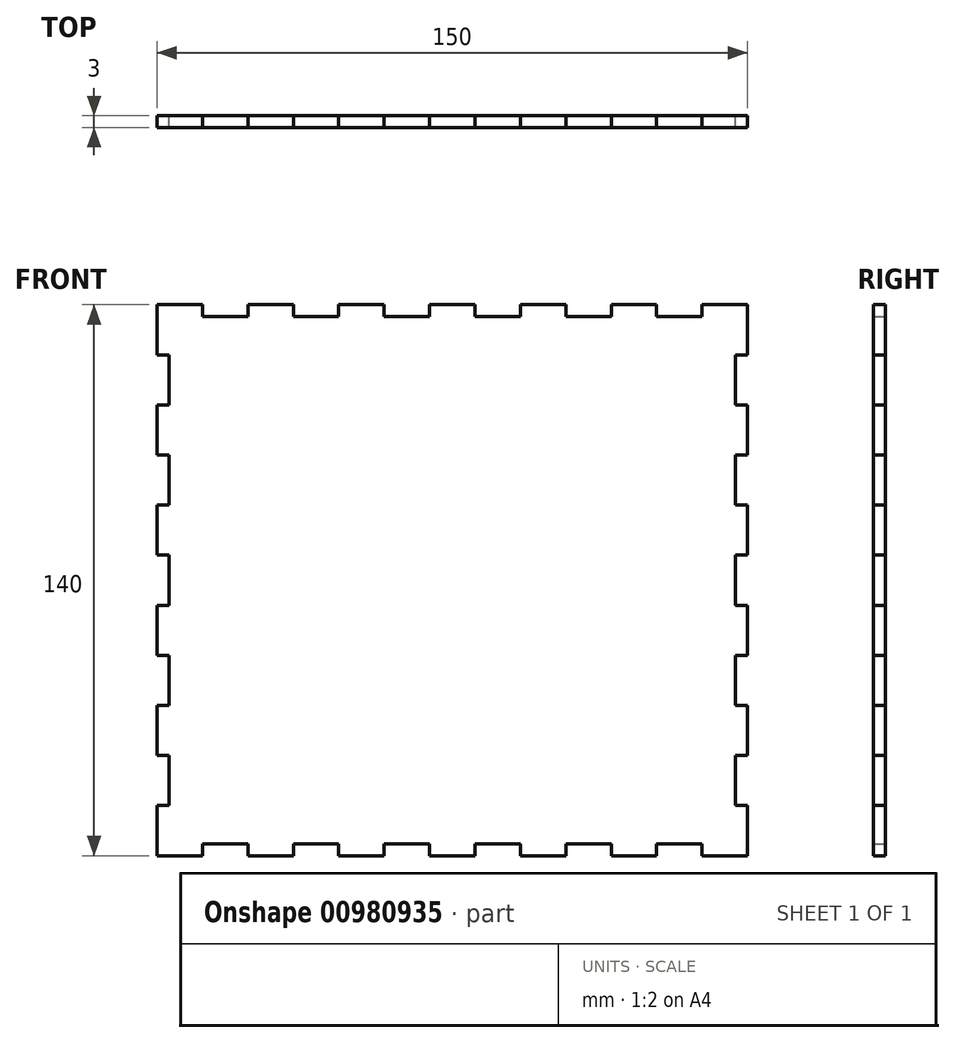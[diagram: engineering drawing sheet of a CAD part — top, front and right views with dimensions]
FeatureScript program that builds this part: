
annotation { "Feature Type Name" : "Feature", "Feature Type Description" : "" }
export const myFeature = defineFeature(function(context is Context, id is Id, definition is map)
    precondition{}
    {
        {
            var Q0;
            Q0=qCreatedBy(makeId("Front.planeOp"),FACE);
            var sketch = newSketch(context, id + "F0", { "sketchPlane" : qUnion([Q0])});
            skPoint(sketch, "E0.middle", {"position": v(0, 0) * mm});
            skLineSegment(sketch, "E1", {"start": v(75, 70) * mm, "end": v(75, 57.27) * mm});
            skLineSegment(sketch, "E2", {"start": v(75, 57.27) * mm, "end": v(72, 57.27) * mm});
            skLineSegment(sketch, "E3", {"start": v(72, 57.27) * mm, "end": v(72, 44.55) * mm});
            skLineSegment(sketch, "E4", {"start": v(72, 44.55) * mm, "end": v(75, 44.55) * mm});
            skLineSegment(sketch, "E5", {"start": v(75, 44.55) * mm, "end": v(75, 31.82) * mm});
            skLineSegment(sketch, "E6.1.0.1", {"start": v(75, 19.1) * mm, "end": v(75, 6.36) * mm});
            skLineSegment(sketch, "E6.1.0.2", {"start": v(72, 31.82) * mm, "end": v(72, 19.1) * mm});
            skLineSegment(sketch, "E6.1.0.3", {"start": v(72, 19.1) * mm, "end": v(75, 19.1) * mm});
            skLineSegment(sketch, "E6.1.0.4", {"start": v(75, 31.82) * mm, "end": v(72, 31.82) * mm});
            skLineSegment(sketch, "E6.2.0.0", {"start": v(75, 19.1) * mm, "end": v(75, 6.36) * mm});
            skLineSegment(sketch, "E6.2.0.1", {"start": v(75, -6.36) * mm, "end": v(75, -19.1) * mm});
            skLineSegment(sketch, "E6.2.0.2", {"start": v(72, 6.36) * mm, "end": v(72, -6.36) * mm});
            skLineSegment(sketch, "E6.2.0.3", {"start": v(72, -6.36) * mm, "end": v(75, -6.36) * mm});
            skLineSegment(sketch, "E6.2.0.4", {"start": v(75, 6.36) * mm, "end": v(72, 6.36) * mm});
            skLineSegment(sketch, "E6.3.0.0", {"start": v(75, -6.36) * mm, "end": v(75, -19.1) * mm});
            skLineSegment(sketch, "E6.3.0.1", {"start": v(75, -31.82) * mm, "end": v(75, -44.55) * mm});
            skLineSegment(sketch, "E6.3.0.2", {"start": v(72, -19.1) * mm, "end": v(72, -31.82) * mm});
            skLineSegment(sketch, "E6.3.0.3", {"start": v(72, -31.82) * mm, "end": v(75, -31.82) * mm});
            skLineSegment(sketch, "E6.3.0.4", {"start": v(75, -19.1) * mm, "end": v(72, -19.1) * mm});
            skLineSegment(sketch, "E6.4.0.0", {"start": v(75, -31.82) * mm, "end": v(75, -44.55) * mm});
            skLineSegment(sketch, "E6.4.0.1", {"start": v(75, -57.27) * mm, "end": v(75, -70) * mm});
            skLineSegment(sketch, "E6.4.0.2", {"start": v(72, -44.55) * mm, "end": v(72, -57.27) * mm});
            skLineSegment(sketch, "E6.4.0.3", {"start": v(72, -57.27) * mm, "end": v(75, -57.27) * mm});
            skLineSegment(sketch, "E6.4.0.4", {"start": v(75, -44.55) * mm, "end": v(72, -44.55) * mm});
            skLineSegment(sketch, "E6.direction1", {"start": v(75, 70) * mm, "end": v(75, 44.55) * mm, "construction": true});
            skLineSegment(sketch, "E7.MirrorCS", {"start": v(-75, 70) * mm, "end": v(-75, 57.27) * mm});
            skLineSegment(sketch, "E8.MirrorCS", {"start": v(-75, -31.82) * mm, "end": v(-75, -44.55) * mm});
            skLineSegment(sketch, "E9.MirrorCS", {"start": v(-75, 44.55) * mm, "end": v(-75, 31.82) * mm});
            skLineSegment(sketch, "E10.MirrorCS", {"start": v(-75, 19.1) * mm, "end": v(-75, 6.36) * mm});
            skLineSegment(sketch, "E11.MirrorCS", {"start": v(-75, -6.36) * mm, "end": v(-75, -19.1) * mm});
            skLineSegment(sketch, "E12.MirrorCS", {"start": v(-75, 70) * mm, "end": v(-75, 44.55) * mm, "construction": true});
            skLineSegment(sketch, "E13.MirrorCS", {"start": v(-75, -44.55) * mm, "end": v(-72, -44.55) * mm});
            skLineSegment(sketch, "E14.MirrorCS", {"start": v(-72, -57.27) * mm, "end": v(-75, -57.27) * mm});
            skLineSegment(sketch, "E15.MirrorCS", {"start": v(-72, -44.55) * mm, "end": v(-72, -57.27) * mm});
            skLineSegment(sketch, "E16.MirrorCS", {"start": v(-75, -57.27) * mm, "end": v(-75, -70) * mm});
            skLineSegment(sketch, "E17.MirrorCS", {"start": v(-75, 57.27) * mm, "end": v(-72, 57.27) * mm});
            skLineSegment(sketch, "E18.MirrorCS", {"start": v(-72, 57.27) * mm, "end": v(-72, 44.55) * mm});
            skLineSegment(sketch, "E19.MirrorCS", {"start": v(-72, 6.36) * mm, "end": v(-72, -6.36) * mm});
            skLineSegment(sketch, "E20.MirrorCS", {"start": v(-75, 31.82) * mm, "end": v(-72, 31.82) * mm});
            skLineSegment(sketch, "E21.MirrorCS", {"start": v(-75, 6.36) * mm, "end": v(-72, 6.36) * mm});
            skLineSegment(sketch, "E22.MirrorCS", {"start": v(-75, -19.1) * mm, "end": v(-72, -19.1) * mm});
            skLineSegment(sketch, "E23.MirrorCS", {"start": v(-72, -19.1) * mm, "end": v(-72, -31.82) * mm});
            skLineSegment(sketch, "E24.MirrorCS", {"start": v(-72, -6.36) * mm, "end": v(-75, -6.36) * mm});
            skLineSegment(sketch, "E25.MirrorCS", {"start": v(-72, -31.82) * mm, "end": v(-75, -31.82) * mm});
            skLineSegment(sketch, "E26.MirrorCS", {"start": v(-72, 31.82) * mm, "end": v(-72, 19.1) * mm});
            skLineSegment(sketch, "E27.MirrorCS", {"start": v(-72, 44.55) * mm, "end": v(-75, 44.55) * mm});
            skLineSegment(sketch, "E28.MirrorCS", {"start": v(-72, 19.1) * mm, "end": v(-75, 19.1) * mm});
            skLineSegment(sketch, "E29", {"start": v(-75, 70) * mm, "end": v(-63.46, 70) * mm});
            skLineSegment(sketch, "E30", {"start": v(-63.46, 70) * mm, "end": v(-63.46, 67) * mm});
            skLineSegment(sketch, "E31", {"start": v(-63.46, 67) * mm, "end": v(-51.92, 67) * mm});
            skLineSegment(sketch, "E32", {"start": v(-51.92, 67) * mm, "end": v(-51.92, 70) * mm});
            skLineSegment(sketch, "E33", {"start": v(-51.92, 70) * mm, "end": v(-40.38, 70) * mm});
            skLineSegment(sketch, "E34.1.0.1", {"start": v(-28.85, 70) * mm, "end": v(-17.3, 70) * mm});
            skLineSegment(sketch, "E34.1.0.3", {"start": v(-28.85, 67) * mm, "end": v(-28.85, 70) * mm});
            skLineSegment(sketch, "E34.1.0.4", {"start": v(-40.38, 70) * mm, "end": v(-40.38, 67) * mm});
            skLineSegment(sketch, "E34.1.0.5", {"start": v(-40.38, 67) * mm, "end": v(-28.85, 67) * mm});
            skLineSegment(sketch, "E34.2.0.1", {"start": v(-5.77, 70) * mm, "end": v(5.77, 70) * mm});
            skLineSegment(sketch, "E34.2.0.2", {"start": v(-28.85, 70) * mm, "end": v(-17.3, 70) * mm});
            skLineSegment(sketch, "E34.2.0.3", {"start": v(-5.77, 67) * mm, "end": v(-5.77, 70) * mm});
            skLineSegment(sketch, "E34.2.0.4", {"start": v(-17.3, 70) * mm, "end": v(-17.3, 67) * mm});
            skLineSegment(sketch, "E34.2.0.5", {"start": v(-17.3, 67) * mm, "end": v(-5.77, 67) * mm});
            skLineSegment(sketch, "E34.3.0.1", {"start": v(17.3, 70) * mm, "end": v(28.85, 70) * mm});
            skLineSegment(sketch, "E34.3.0.2", {"start": v(-5.77, 70) * mm, "end": v(5.77, 70) * mm});
            skLineSegment(sketch, "E34.3.0.3", {"start": v(17.3, 67) * mm, "end": v(17.3, 70) * mm});
            skLineSegment(sketch, "E34.3.0.4", {"start": v(5.77, 70) * mm, "end": v(5.77, 67) * mm});
            skLineSegment(sketch, "E34.3.0.5", {"start": v(5.77, 67) * mm, "end": v(17.3, 67) * mm});
            skLineSegment(sketch, "E34.4.0.1", {"start": v(40.38, 70) * mm, "end": v(51.92, 70) * mm});
            skLineSegment(sketch, "E34.4.0.2", {"start": v(17.3, 70) * mm, "end": v(28.85, 70) * mm});
            skLineSegment(sketch, "E34.4.0.3", {"start": v(40.38, 67) * mm, "end": v(40.38, 70) * mm});
            skLineSegment(sketch, "E34.4.0.4", {"start": v(28.85, 70) * mm, "end": v(28.85, 67) * mm});
            skLineSegment(sketch, "E34.4.0.5", {"start": v(28.85, 67) * mm, "end": v(40.38, 67) * mm});
            skLineSegment(sketch, "E34.5.0.1", {"start": v(63.46, 70) * mm, "end": v(75, 70) * mm});
            skLineSegment(sketch, "E34.5.0.2", {"start": v(40.38, 70) * mm, "end": v(51.92, 70) * mm});
            skLineSegment(sketch, "E34.5.0.3", {"start": v(63.46, 67) * mm, "end": v(63.46, 70) * mm});
            skLineSegment(sketch, "E34.5.0.4", {"start": v(51.92, 70) * mm, "end": v(51.92, 67) * mm});
            skLineSegment(sketch, "E34.5.0.5", {"start": v(51.92, 67) * mm, "end": v(63.46, 67) * mm});
            skLineSegment(sketch, "E34.direction1", {"start": v(-75, 70) * mm, "end": v(-51.92, 70) * mm, "construction": true});
            skLineSegment(sketch, "E35.MirrorCS", {"start": v(40.38, -70) * mm, "end": v(51.92, -70) * mm});
            skLineSegment(sketch, "E36.MirrorCS", {"start": v(-5.77, -70) * mm, "end": v(5.77, -70) * mm});
            skLineSegment(sketch, "E37.MirrorCS", {"start": v(-51.92, -70) * mm, "end": v(-40.38, -70) * mm});
            skLineSegment(sketch, "E38.MirrorCS", {"start": v(-75, -70) * mm, "end": v(-63.46, -70) * mm});
            skLineSegment(sketch, "E39.MirrorCS", {"start": v(-28.85, -70) * mm, "end": v(-17.3, -70) * mm});
            skLineSegment(sketch, "E40.MirrorCS", {"start": v(17.3, -70) * mm, "end": v(28.85, -70) * mm});
            skLineSegment(sketch, "E41.MirrorCS", {"start": v(-63.46, -67) * mm, "end": v(-51.92, -67) * mm});
            skLineSegment(sketch, "E42.MirrorCS", {"start": v(-51.92, -67) * mm, "end": v(-51.92, -70) * mm});
            skLineSegment(sketch, "E43.MirrorCS", {"start": v(-17.3, -67) * mm, "end": v(-5.77, -67) * mm});
            skLineSegment(sketch, "E44.MirrorCS", {"start": v(40.38, -67) * mm, "end": v(40.38, -70) * mm});
            skLineSegment(sketch, "E45.MirrorCS", {"start": v(-17.3, -70) * mm, "end": v(-17.3, -67) * mm});
            skLineSegment(sketch, "E46.MirrorCS", {"start": v(-40.38, -67) * mm, "end": v(-28.85, -67) * mm});
            skLineSegment(sketch, "E47.MirrorCS", {"start": v(28.85, -70) * mm, "end": v(28.85, -67) * mm});
            skLineSegment(sketch, "E48.MirrorCS", {"start": v(-75, -70) * mm, "end": v(-51.92, -70) * mm, "construction": true});
            skLineSegment(sketch, "E49.MirrorCS", {"start": v(-28.85, -67) * mm, "end": v(-28.85, -70) * mm});
            skLineSegment(sketch, "E50.MirrorCS", {"start": v(-5.77, -67) * mm, "end": v(-5.77, -70) * mm});
            skLineSegment(sketch, "E51.MirrorCS", {"start": v(28.85, -67) * mm, "end": v(40.38, -67) * mm});
            skLineSegment(sketch, "E52.MirrorCS", {"start": v(-63.46, -70) * mm, "end": v(-63.46, -67) * mm});
            skLineSegment(sketch, "E53.MirrorCS", {"start": v(63.46, -70) * mm, "end": v(75, -70) * mm});
            skLineSegment(sketch, "E54.MirrorCS", {"start": v(-40.38, -70) * mm, "end": v(-40.38, -67) * mm});
            skLineSegment(sketch, "E55.MirrorCS", {"start": v(51.92, -67) * mm, "end": v(63.46, -67) * mm});
            skLineSegment(sketch, "E56.MirrorCS", {"start": v(5.77, -70) * mm, "end": v(5.77, -67) * mm});
            skLineSegment(sketch, "E57.MirrorCS", {"start": v(17.3, -67) * mm, "end": v(17.3, -70) * mm});
            skLineSegment(sketch, "E58.MirrorCS", {"start": v(5.77, -67) * mm, "end": v(17.3, -67) * mm});
            skLineSegment(sketch, "E59.MirrorCS", {"start": v(63.46, -67) * mm, "end": v(63.46, -70) * mm});
            skLineSegment(sketch, "E60.MirrorCS", {"start": v(51.92, -70) * mm, "end": v(51.92, -67) * mm});
            skSolve(sketch);
        }
        {
            var Q0;
            Q0=makeQuery(id+"F0.imprint","IMPRINT",FACE,{"disambiguationData":[TD([[makeQuery(id+"F0.imprint","IMPRINT",EDGE,{"derivedFrom":sQuery(id+"F0.wireOp",EDGE,"E1")}),-1.0]])]});
            extrude(context, id + "F1", {"entities" : qUnion([Q0]), "depth" : 3 * mm, "offsetDistance" : 25 * mm});
        }
    });
